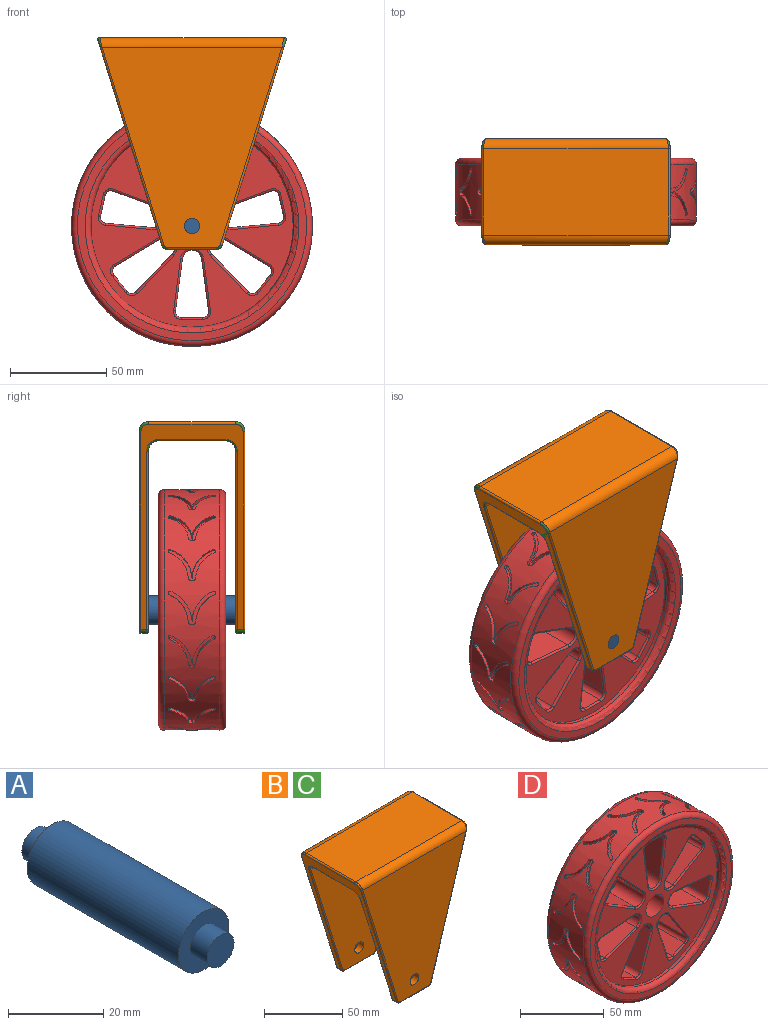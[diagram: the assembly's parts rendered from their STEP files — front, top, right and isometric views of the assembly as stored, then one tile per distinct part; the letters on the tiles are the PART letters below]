
ASSEMBLY  parts=4 mates=2
PART A: 7 faces, bbox 15x55x15 mm
  f0: cylinder r=7.49mm len=45mm, axis (0,1,0), area 2117.7mm2, adj f1,f2
  f1: plane 14.98x14.98mm, normal (0,-1,0), area 126mm2, adj f0,f5
  f2: plane 14.98x14.98mm, normal (0,1,0), area 126mm2, adj f0,f4
  f3: plane 8x8mm, normal (0,1,0), area 50.3mm2, adj f4
  f4: cylinder r=4mm len=8mm, axis (0,1,0), area 125.7mm2, adj f2,f3
  f5: cylinder r=4mm len=8mm, axis (0,1,0), area 125.7mm2, adj f1,f6
  f6: plane 8x8mm, normal (0,-1,0), area 50.3mm2, adj f5
PART B: 52 faces, bbox 98.5x55x110.2 mm
  f0: cylinder r=3mm len=3mm, axis (0,1,0), area 11.4mm2, adj f3,f5,f32,f46
  f1: cylinder r=3mm len=3mm, axis (0,1,0), area 11.4mm2, adj f3,f7,f28,f50
  f2: cylinder r=4.01mm len=8.02mm, axis (0,1,0), area 126mm2, adj f12,f15
  f3: plane 25.52x3mm, normal (0,0,-1), area 76.6mm2, adj f0,f1,f30,f48
  f4: cylinder r=3mm len=3mm, axis (0,1,0), area 11.4mm2, adj f5,f10,f27,f37
  f5: plane 106.6x53mm, normal (0.95,0,-0.3), area 1072.7mm2, adj f0,f4,f29,f31,f33,f34,f35,f36
  f6: plane 95.78x45mm, normal (0,0,1), area 4310mm2, adj f18,f19,f40,f47
  f7: plane 106.6x53mm, normal (-0.95,0,-0.3), area 1072.7mm2, adj f1,f8,f20,f21,f22,f24,f26,f43
  f8: cylinder r=3mm len=3mm, axis (0,1,0), area 11.4mm2, adj f7,f10,f23,f41
  f9: cylinder r=4.01mm len=8.02mm, axis (0,1,0), area 126mm2, adj f11,f14
  f10: plane 25.52x3mm, normal (0,0,-1), area 76.6mm2, adj f4,f8,f25,f39
  f11: plane 104x93.29mm, normal (0,-1,0), area 6279.7mm2, adj f9,f19,f36,f37,f39,f41,f43
  f12: plane 104x93.29mm, normal (0,1,0), area 6279.7mm2, adj f2,f18,f44,f46,f48,f50,f51
  f13: plane 90.79x35mm, normal (0,0,-1), area 3177.7mm2, adj f16,f17,f22,f33
  f14: plane 94x87.05mm, normal (0,1,0), area 5378mm2, adj f9,f17,f21,f23,f25,f27,f29
  f15: plane 94x87.05mm, normal (0,-1,0), area 5378mm2, adj f2,f16,f26,f28,f30,f32,f34
  f16: cylinder r=5mm len=90.79mm, axis (-1,0,0), area 702.4mm2, adj f13,f15,f24,f35
  f17: cylinder r=5mm len=90.79mm, axis (1,0,0), area 702.4mm2, adj f13,f14,f20,f31
  f18: cylinder r=5mm len=95.78mm, axis (-1,0,0), area 745.1mm2, adj f6,f12,f42,f49
  f19: cylinder r=5mm len=95.78mm, axis (1,0,0), area 745.1mm2, adj f6,f11,f38,f45
  f20: bspline ~6x6mm, area 12.1mm2, adj f7,f17,f21,f22
  f21: cylinder r=1mm len=92.89mm, axis (0.3,0,-0.95), area 152.3mm2, adj f7,f14,f20,f23
  f22: cylinder r=1mm len=35mm, axis (0,-1,0), area 44.4mm2, adj f7,f13,f20,f24
  f23: torus R=2mm, axis (0,-1,0), area 5.3mm2, adj f8,f14,f21,f25
  f24: bspline ~6x6mm, area 12.1mm2, adj f7,f16,f22,f26
  f25: cylinder r=1mm len=25.52mm, axis (1,0,0), area 40.1mm2, adj f10,f14,f23,f27
  f26: cylinder r=1mm len=92.89mm, axis (-0.3,0,0.95), area 152.3mm2, adj f7,f15,f24,f28
  f27: torus R=2mm, axis (0,-1,0), area 5.3mm2, adj f4,f14,f25,f29
  f28: torus R=2mm, axis (0,-1,0), area 5.3mm2, adj f1,f15,f26,f30
  f29: cylinder r=1mm len=92.89mm, axis (0.3,0,0.95), area 152.3mm2, adj f5,f14,f27,f31
  f30: cylinder r=1mm len=25.52mm, axis (-1,0,0), area 40.1mm2, adj f3,f15,f28,f32
  f31: bspline ~6x6mm, area 12.1mm2, adj f5,f17,f29,f33
  f32: torus R=2mm, axis (0,-1,0), area 5.3mm2, adj f0,f15,f30,f34
  f33: cylinder r=1mm len=35mm, axis (0,1,0), area 44.4mm2, adj f5,f13,f31,f35
  f34: cylinder r=1mm len=92.89mm, axis (-0.3,0,-0.95), area 152.3mm2, adj f5,f15,f32,f35
  f35: bspline ~6x6mm, area 12.1mm2, adj f5,f16,f33,f34
  f36: cylinder r=1mm len=102.89mm, axis (-0.3,0,-0.95), area 168.8mm2, adj f5,f11,f37,f38
  f37: torus R=2mm, axis (0,-1,0), area 5.3mm2, adj f4,f11,f36,f39
  f38: bspline ~6.14x5.01mm, area 13.2mm2, adj f5,f19,f36,f40
  f39: cylinder r=1mm len=25.52mm, axis (-1,0,0), area 40.1mm2, adj f10,f11,f37,f41
  f40: cylinder r=1mm len=45mm, axis (0,-1,0), area 84.3mm2, adj f5,f6,f38,f42
  f41: torus R=2mm, axis (0,-1,0), area 5.3mm2, adj f8,f11,f39,f43
  f42: bspline ~5.3x5mm, area 13.2mm2, adj f5,f18,f40,f44
  f43: cylinder r=1mm len=102.89mm, axis (-0.3,0,0.95), area 168.8mm2, adj f7,f11,f41,f45
  f44: cylinder r=1mm len=102.89mm, axis (0.3,0,0.95), area 168.8mm2, adj f5,f12,f42,f46
  f45: bspline ~6.14x5.96mm, area 13.2mm2, adj f7,f19,f43,f47
  f46: torus R=2mm, axis (0,-1,0), area 5.3mm2, adj f0,f12,f44,f48
  f47: cylinder r=1mm len=45mm, axis (0,1,0), area 84.3mm2, adj f6,f7,f45,f49
  f48: cylinder r=1mm len=25.52mm, axis (1,0,0), area 40.1mm2, adj f3,f12,f46,f50
  f49: bspline ~6.14x5.01mm, area 13.2mm2, adj f7,f18,f47,f51
  f50: torus R=2mm, axis (0,-1,0), area 5.3mm2, adj f1,f12,f48,f51
  f51: cylinder r=1mm len=102.89mm, axis (0.3,0,-0.95), area 168.8mm2, adj f7,f12,f49,f50
PART C: same geometry as B
PART D: 275 faces, bbox 135.3x35x135.3 mm
  f0: plane 27.26x23mm, normal (0.99,0,0.13), area 632.5mm2, adj f1,f35,f48,f90
  f1: cylinder r=3mm len=23mm, axis (0,1,0), area 117.5mm2, adj f0,f2,f46,f88
  f2: plane 23x11.19mm, normal (0,0,-1), area 257.4mm2, adj f1,f3,f45,f87
  f3: cylinder r=3mm len=23mm, axis (0,1,0), area 117.5mm2, adj f2,f4,f47,f89
  f4: plane 27.26x23mm, normal (-0.99,0,0.13), area 632.5mm2, adj f3,f35,f49,f91
  f5: cylinder r=5mm len=23mm, axis (0,1,0), area 331mm2, adj f6,f36,f55,f97
  f6: plane 23.57x23mm, normal (0.52,0,0.86), area 632.5mm2, adj f5,f7,f53,f95
  f7: cylinder r=3mm len=23mm, axis (0,1,0), area 117.5mm2, adj f6,f8,f51,f93
  f8: plane 23x8.75mm, normal (0.78,0,-0.62), area 257.4mm2, adj f7,f9,f52,f94
  f9: cylinder r=3mm len=23mm, axis (0,1,0), area 117.5mm2, adj f8,f36,f54,f96
  f10: cylinder r=5mm len=23mm, axis (0,1,0), area 331mm2, adj f11,f37,f61,f103
  f11: plane 25.78x23mm, normal (-0.35,0,0.94), area 632.5mm2, adj f10,f12,f59,f101
  f12: cylinder r=3mm len=23mm, axis (0,1,0), area 117.5mm2, adj f11,f13,f57,f99
  f13: plane 23x10.91mm, normal (0.97,0,0.22), area 257.4mm2, adj f12,f14,f58,f100
  f14: cylinder r=3mm len=23mm, axis (0,1,0), area 117.5mm2, adj f13,f37,f60,f102
  f15: cylinder r=5mm len=23mm, axis (0,1,0), area 331mm2, adj f16,f38,f67,f109
  f16: plane 26.13x23mm, normal (-0.95,0,0.31), area 632.5mm2, adj f15,f17,f65,f107
  f17: cylinder r=3mm len=23mm, axis (0,1,0), area 117.5mm2, adj f16,f18,f63,f105
  f18: plane 23x10.08mm, normal (0.43,0,0.9), area 257.4mm2, adj f17,f19,f64,f106
  f19: cylinder r=3mm len=23mm, axis (0,1,0), area 117.5mm2, adj f18,f38,f66,f108
  f20: cylinder r=5mm len=23mm, axis (0,1,0), area 331mm2, adj f21,f39,f73,f115
  f21: plane 23x23mm, normal (-0.84,0,-0.55), area 632.5mm2, adj f20,f22,f71,f113
  f22: cylinder r=3mm len=23mm, axis (0,1,0), area 117.5mm2, adj f21,f23,f69,f111
  f23: plane 23x10.08mm, normal (-0.43,0,0.9), area 257.4mm2, adj f22,f24,f70,f112
  f24: cylinder r=3mm len=23mm, axis (0,1,0), area 117.5mm2, adj f23,f39,f72,f114
  f25: cylinder r=5mm len=23mm, axis (0,1,0), area 331mm2, adj f26,f40,f79,f121
  f26: plane 27.38x23mm, normal (-0.09,0,-1), area 632.5mm2, adj f25,f27,f77,f119
  f27: cylinder r=3mm len=23mm, axis (0,1,0), area 117.5mm2, adj f26,f28,f75,f117
  f28: plane 23x10.91mm, normal (-0.97,0,0.22), area 257.4mm2, adj f27,f29,f76,f118
  f29: cylinder r=3mm len=23mm, axis (0,1,0), area 117.5mm2, adj f28,f40,f78,f120
  f30: cylinder r=5mm len=23mm, axis (0,1,0), area 331mm2, adj f31,f41,f85,f127
  f31: plane 23x19.82mm, normal (0.72,0,-0.69), area 632.5mm2, adj f30,f32,f83,f125
  f32: cylinder r=3mm len=23mm, axis (0,1,0), area 117.5mm2, adj f31,f33,f81,f123
  f33: plane 23x8.75mm, normal (-0.78,0,-0.62), area 257.4mm2, adj f32,f34,f82,f124
  f34: cylinder r=3mm len=23mm, axis (0,1,0), area 117.5mm2, adj f33,f41,f84,f126
  f35: cylinder r=5mm len=23mm, axis (0,1,0), area 331mm2, adj f0,f4,f50,f92
  f36: plane 23x19.82mm, normal (-0.72,0,-0.69), area 632.5mm2, adj f5,f9,f56,f98
  f37: plane 27.38x23mm, normal (0.09,0,-1), area 632.5mm2, adj f10,f14,f62,f104
  f38: plane 23x23mm, normal (0.84,0,-0.55), area 632.5mm2, adj f15,f19,f68,f110
  f39: plane 26.13x23mm, normal (0.95,0,0.31), area 632.5mm2, adj f20,f24,f74,f116
  f40: plane 25.78x23mm, normal (0.35,0,0.94), area 632.5mm2, adj f25,f29,f80,f122
  f41: plane 23.57x23mm, normal (-0.52,0,0.86), area 632.5mm2, adj f30,f34,f86,f128
  f42: cylinder r=7.5mm len=25mm, axis (0,1,0), area 1178.1mm2, adj f43,f44
  f43: plane 105x105mm, normal (0,-1,0), area 4633.1mm2, adj f42,f87,f88,f89,f90,f91,f92,f93
  f44: plane 105x105mm, normal (0,1,0), area 4633.1mm2, adj f42,f45,f46,f47,f48,f49,f50,f51
  f45: cylinder r=1mm len=11.19mm, axis (1,0,0), area 17.6mm2, adj f2,f44,f46,f47
  f46: torus R=4mm, axis (0,-1,0), area 9mm2, adj f1,f44,f45,f48
  f47: torus R=4mm, axis (0,-1,0), area 9mm2, adj f3,f44,f45,f49
  f48: cylinder r=1mm len=27.39mm, axis (-0.13,0,0.99), area 43.2mm2, adj f0,f44,f46,f50
  f49: cylinder r=1mm len=27.39mm, axis (-0.13,0,-0.99), area 43.2mm2, adj f4,f44,f47,f50
  f50: torus R=6mm, axis (0,-1,0), area 24.2mm2, adj f35,f44,f48,f49
  f51: torus R=4mm, axis (0,-1,0), area 9mm2, adj f7,f44,f52,f53
  f52: cylinder r=1mm len=9.37mm, axis (0.62,0,0.78), area 17.6mm2, adj f8,f44,f51,f54
  f53: cylinder r=1mm len=24.08mm, axis (-0.86,0,0.52), area 43.2mm2, adj f6,f44,f51,f55
  f54: torus R=4mm, axis (0,-1,0), area 9mm2, adj f9,f44,f52,f56
  f55: torus R=6mm, axis (0,-1,0), area 24.2mm2, adj f5,f44,f53,f56
  f56: cylinder r=1mm len=20.52mm, axis (0.69,0,-0.72), area 43.2mm2, adj f36,f44,f54,f55
  f57: torus R=4mm, axis (0,-1,0), area 9mm2, adj f12,f44,f58,f59
  f58: cylinder r=1mm len=11.13mm, axis (-0.22,0,0.97), area 17.6mm2, adj f13,f44,f57,f60
  f59: cylinder r=1mm len=26.12mm, axis (-0.94,0,-0.35), area 43.2mm2, adj f11,f44,f57,f61
  f60: torus R=4mm, axis (0,-1,0), area 9mm2, adj f14,f44,f58,f62
  f61: torus R=6mm, axis (0,-1,0), area 24.2mm2, adj f10,f44,f59,f62
  f62: cylinder r=1mm len=27.48mm, axis (1,0,0.09), area 43.2mm2, adj f37,f44,f60,f61
  f63: torus R=4mm, axis (0,-1,0), area 9mm2, adj f17,f44,f64,f65
  f64: cylinder r=1mm len=10.52mm, axis (-0.9,0,0.43), area 17.6mm2, adj f18,f44,f63,f66
  f65: cylinder r=1mm len=26.44mm, axis (-0.31,0,-0.95), area 43.2mm2, adj f16,f44,f63,f67
  f66: torus R=4mm, axis (0,-1,0), area 9mm2, adj f19,f44,f64,f68
  f67: torus R=6mm, axis (0,-1,0), area 24.2mm2, adj f15,f44,f65,f68
  f68: cylinder r=1mm len=23.54mm, axis (0.55,0,0.84), area 43.2mm2, adj f38,f44,f66,f67
  f69: torus R=4mm, axis (0,-1,0), area 9mm2, adj f22,f44,f70,f71
  f70: cylinder r=1mm len=10.52mm, axis (-0.9,0,-0.43), area 17.6mm2, adj f23,f44,f69,f72
  f71: cylinder r=1mm len=23.54mm, axis (0.55,0,-0.84), area 43.2mm2, adj f21,f44,f69,f73
  f72: torus R=4mm, axis (0,-1,0), area 9mm2, adj f24,f44,f70,f74
  f73: torus R=6mm, axis (0,-1,0), area 24.2mm2, adj f20,f44,f71,f74
  f74: cylinder r=1mm len=26.44mm, axis (-0.31,0,0.95), area 43.2mm2, adj f39,f44,f72,f73
  f75: torus R=4mm, axis (0,-1,0), area 9mm2, adj f27,f44,f76,f77
  f76: cylinder r=1mm len=11.13mm, axis (-0.22,0,-0.97), area 17.6mm2, adj f28,f44,f75,f78
  f77: cylinder r=1mm len=27.48mm, axis (1,0,-0.09), area 43.2mm2, adj f26,f44,f75,f79
  f78: torus R=4mm, axis (0,-1,0), area 9mm2, adj f29,f44,f76,f80
  f79: torus R=6mm, axis (0,-1,0), area 24.2mm2, adj f25,f44,f77,f80
  f80: cylinder r=1mm len=26.12mm, axis (-0.94,0,0.35), area 43.2mm2, adj f40,f44,f78,f79
  f81: torus R=4mm, axis (0,-1,0), area 9mm2, adj f32,f44,f82,f83
  f82: cylinder r=1mm len=9.37mm, axis (0.62,0,-0.78), area 17.6mm2, adj f33,f44,f81,f84
  f83: cylinder r=1mm len=20.52mm, axis (0.69,0,0.72), area 43.2mm2, adj f31,f44,f81,f85
  f84: torus R=4mm, axis (0,-1,0), area 9mm2, adj f34,f44,f82,f86
  f85: torus R=6mm, axis (0,-1,0), area 24.2mm2, adj f30,f44,f83,f86
  f86: cylinder r=1mm len=24.08mm, axis (-0.86,0,-0.52), area 43.2mm2, adj f41,f44,f84,f85
  f87: cylinder r=1mm len=11.19mm, axis (-1,0,0), area 17.6mm2, adj f2,f43,f88,f89
  f88: torus R=4mm, axis (0,-1,0), area 9mm2, adj f1,f43,f87,f90
  f89: torus R=4mm, axis (0,-1,0), area 9mm2, adj f3,f43,f87,f91
  f90: cylinder r=1mm len=27.39mm, axis (0.13,0,-0.99), area 43.2mm2, adj f0,f43,f88,f92
  f91: cylinder r=1mm len=27.39mm, axis (0.13,0,0.99), area 43.2mm2, adj f4,f43,f89,f92
  f92: torus R=6mm, axis (0,-1,0), area 24.2mm2, adj f35,f43,f90,f91
  f93: torus R=4mm, axis (0,-1,0), area 9mm2, adj f7,f43,f94,f95
  f94: cylinder r=1mm len=9.37mm, axis (-0.62,0,-0.78), area 17.6mm2, adj f8,f43,f93,f96
  f95: cylinder r=1mm len=24.08mm, axis (0.86,0,-0.52), area 43.2mm2, adj f6,f43,f93,f97
  f96: torus R=4mm, axis (0,-1,0), area 9mm2, adj f9,f43,f94,f98
  f97: torus R=6mm, axis (0,-1,0), area 24.2mm2, adj f5,f43,f95,f98
  f98: cylinder r=1mm len=20.52mm, axis (-0.69,0,0.72), area 43.2mm2, adj f36,f43,f96,f97
  f99: torus R=4mm, axis (0,-1,0), area 9mm2, adj f12,f43,f100,f101
  f100: cylinder r=1mm len=11.13mm, axis (0.22,0,-0.97), area 17.6mm2, adj f13,f43,f99,f102
  f101: cylinder r=1mm len=26.12mm, axis (0.94,0,0.35), area 43.2mm2, adj f11,f43,f99,f103
  f102: torus R=4mm, axis (0,-1,0), area 9mm2, adj f14,f43,f100,f104
  f103: torus R=6mm, axis (0,-1,0), area 24.2mm2, adj f10,f43,f101,f104
  f104: cylinder r=1mm len=27.48mm, axis (-1,0,-0.09), area 43.2mm2, adj f37,f43,f102,f103
  f105: torus R=4mm, axis (0,-1,0), area 9mm2, adj f17,f43,f106,f107
  f106: cylinder r=1mm len=10.52mm, axis (0.9,0,-0.43), area 17.6mm2, adj f18,f43,f105,f108
  f107: cylinder r=1mm len=26.44mm, axis (0.31,0,0.95), area 43.2mm2, adj f16,f43,f105,f109
  f108: torus R=4mm, axis (0,-1,0), area 9mm2, adj f19,f43,f106,f110
  f109: torus R=6mm, axis (0,-1,0), area 24.2mm2, adj f15,f43,f107,f110
  f110: cylinder r=1mm len=23.54mm, axis (-0.55,0,-0.84), area 43.2mm2, adj f38,f43,f108,f109
  f111: torus R=4mm, axis (0,-1,0), area 9mm2, adj f22,f43,f112,f113
  f112: cylinder r=1mm len=10.52mm, axis (0.9,0,0.43), area 17.6mm2, adj f23,f43,f111,f114
  f113: cylinder r=1mm len=23.54mm, axis (-0.55,0,0.84), area 43.2mm2, adj f21,f43,f111,f115
  f114: torus R=4mm, axis (0,-1,0), area 9mm2, adj f24,f43,f112,f116
  f115: torus R=6mm, axis (0,-1,0), area 24.2mm2, adj f20,f43,f113,f116
  f116: cylinder r=1mm len=26.44mm, axis (0.31,0,-0.95), area 43.2mm2, adj f39,f43,f114,f115
  f117: torus R=4mm, axis (0,-1,0), area 9mm2, adj f27,f43,f118,f119
  f118: cylinder r=1mm len=11.13mm, axis (0.22,0,0.97), area 17.6mm2, adj f28,f43,f117,f120
  f119: cylinder r=1mm len=27.48mm, axis (-1,0,0.09), area 43.2mm2, adj f26,f43,f117,f121
  f120: torus R=4mm, axis (0,-1,0), area 9mm2, adj f29,f43,f118,f122
  f121: torus R=6mm, axis (0,-1,0), area 24.2mm2, adj f25,f43,f119,f122
  f122: cylinder r=1mm len=26.12mm, axis (0.94,0,-0.35), area 43.2mm2, adj f40,f43,f120,f121
  f123: torus R=4mm, axis (0,-1,0), area 9mm2, adj f32,f43,f124,f125
  f124: cylinder r=1mm len=9.37mm, axis (-0.62,0,0.78), area 17.6mm2, adj f33,f43,f123,f126
  f125: cylinder r=1mm len=20.52mm, axis (-0.69,0,-0.72), area 43.2mm2, adj f31,f43,f123,f127
  f126: torus R=4mm, axis (0,-1,0), area 9mm2, adj f34,f43,f124,f128
  f127: torus R=6mm, axis (0,-1,0), area 24.2mm2, adj f30,f43,f125,f128
  f128: cylinder r=1mm len=24.08mm, axis (0.86,0,0.52), area 43.2mm2, adj f41,f43,f126,f127
  f129: cylinder r=52.5mm len=105mm, axis (0,1,0), area 659.7mm2, adj f43,f137
  f130: cylinder r=52.5mm len=105mm, axis (0,1,0), area 659.7mm2, adj f44,f135
  f131: cylinder r=62.5mm len=125mm, axis (0,1,0), area 9902.6mm2, adj f132,f136,f138,f139,f140,f141,f142,f143
  f132: cylinder r=62.5mm len=11.48mm, axis (0,1,0), area 40.4mm2, adj f131,f182,f184
  f133: plane 119x119mm, normal (0,-1,0), area 1445.1mm2, adj f137,f138
  f134: plane 119x119mm, normal (0,1,0), area 1445.1mm2, adj f135,f136
  f135: torus R=55.5mm, axis (0,-1,0), area 1586.7mm2, adj f130,f134
  f136: torus R=59.5mm, axis (0,-1,0), area 1818.3mm2, adj f131,f134
  f137: torus R=55.5mm, axis (0,-1,0), area 1586.7mm2, adj f129,f133
  f138: torus R=59.5mm, axis (0,-1,0), area 1818.3mm2, adj f131,f133
  f139: cylinder r=2mm len=3.99mm, axis (0,0,1), area 12mm2, adj f131,f140,f143,f146
  f140: cylinder r=16mm len=13.68mm, axis (0,0,1), area 35.2mm2, adj f131,f139,f141,f146
  f141: cylinder r=1mm len=2.46mm, axis (0,0,1), area 6.3mm2, adj f131,f140,f142,f146
  f142: cylinder r=18mm len=15.39mm, axis (0,0,1), area 39.6mm2, adj f131,f141,f144,f146
  f143: cylinder r=16mm len=13.68mm, axis (0,0,1), area 35.4mm2, adj f131,f139,f145,f146
  f144: cylinder r=18mm len=15.39mm, axis (0,0,1), area 39.8mm2, adj f131,f142,f145,f146
  f145: cylinder r=1mm len=2.46mm, axis (0,0,1), area 6.2mm2, adj f131,f143,f144,f146
  f146: cylinder r=62.5mm len=24.56mm, axis (0,1,0), area 85mm2, adj f139,f140,f141,f142,f143,f144,f145
  f147: cylinder r=2mm len=3.99mm, axis (-1,0,0.09), area 12mm2, adj f131,f148,f151,f154
  f148: cylinder r=16mm len=13.94mm, axis (-1,0,0.09), area 35.2mm2, adj f131,f147,f149,f154
  f149: cylinder r=1mm len=2.62mm, axis (-1,0,0.09), area 6.3mm2, adj f131,f148,f150,f154
  f150: cylinder r=18mm len=15.68mm, axis (-1,0,0.09), area 39.6mm2, adj f131,f149,f152,f154
  f151: cylinder r=16mm len=13.94mm, axis (-1,0,0.09), area 35.4mm2, adj f131,f147,f153,f154
  f152: cylinder r=18mm len=15.68mm, axis (-1,0,0.09), area 39.8mm2, adj f131,f150,f153,f154
  f153: cylinder r=1mm len=2.62mm, axis (-1,0,0.09), area 6.2mm2, adj f131,f151,f152,f154
  f154: cylinder r=62.5mm len=24.56mm, axis (0,1,0), area 85mm2, adj f147,f148,f149,f150,f151,f152,f153
  f155: cylinder r=2mm len=3.99mm, axis (-0.9,0,0.45), area 12mm2, adj f131,f156,f159,f162
  f156: cylinder r=16mm len=13.8mm, axis (-0.9,0,0.45), area 35.2mm2, adj f131,f155,f157,f162
  f157: cylinder r=1mm len=3.05mm, axis (-0.9,0,0.45), area 6.3mm2, adj f131,f156,f158,f162
  f158: cylinder r=18mm len=15.52mm, axis (-0.9,0,0.45), area 39.6mm2, adj f131,f157,f160,f162
  f159: cylinder r=16mm len=13.8mm, axis (-0.9,0,0.45), area 35.4mm2, adj f131,f155,f161,f162
  f160: cylinder r=18mm len=15.52mm, axis (-0.9,0,0.45), area 39.8mm2, adj f131,f158,f161,f162
  f161: cylinder r=1mm len=3.05mm, axis (-0.9,0,0.45), area 6.2mm2, adj f131,f159,f160,f162
  f162: cylinder r=62.5mm len=24.56mm, axis (0,1,0), area 85mm2, adj f155,f156,f157,f158,f159,f160,f161
  f163: cylinder r=2mm len=3.99mm, axis (-0.36,0,0.93), area 12mm2, adj f131,f164,f167,f170
  f164: cylinder r=16mm len=14.01mm, axis (-0.36,0,0.93), area 35.2mm2, adj f131,f163,f165,f170
  f165: cylinder r=1mm len=2.98mm, axis (-0.36,0,0.93), area 6.3mm2, adj f131,f164,f166,f170
  f166: cylinder r=18mm len=15.77mm, axis (-0.36,0,0.93), area 39.6mm2, adj f131,f165,f168,f170
  f167: cylinder r=16mm len=14.01mm, axis (-0.36,0,0.93), area 35.4mm2, adj f131,f163,f169,f170
  f168: cylinder r=18mm len=15.77mm, axis (-0.36,0,0.93), area 39.8mm2, adj f131,f166,f169,f170
  f169: cylinder r=1mm len=2.98mm, axis (-0.36,0,0.93), area 6.2mm2, adj f131,f167,f168,f170
  f170: cylinder r=62.5mm len=24.56mm, axis (0,1,0), area 85mm2, adj f163,f164,f165,f166,f167,f168,f169
  f171: cylinder r=2mm len=3.99mm, axis (-0.67,0,0.74), area 12mm2, adj f131,f172,f175,f178
  f172: cylinder r=16mm len=12.46mm, axis (-0.67,0,0.74), area 35.2mm2, adj f131,f171,f173,f178
  f173: cylinder r=1mm len=3.11mm, axis (-0.67,0,0.74), area 6.3mm2, adj f131,f172,f174,f178
  f174: cylinder r=18mm len=14.02mm, axis (-0.67,0,0.74), area 39.6mm2, adj f131,f173,f176,f178
  f175: cylinder r=16mm len=12.46mm, axis (-0.67,0,0.74), area 35.4mm2, adj f131,f171,f177,f178
  f176: cylinder r=18mm len=14.02mm, axis (-0.67,0,0.74), area 39.8mm2, adj f131,f174,f177,f178
  f177: cylinder r=1mm len=3.11mm, axis (-0.67,0,0.74), area 6.2mm2, adj f131,f175,f176,f178
  f178: cylinder r=62.5mm len=24.56mm, axis (0,1,0), area 85mm2, adj f171,f172,f173,f174,f175,f176,f177
  f179: cylinder r=2mm len=3.99mm, axis (-0.18,0,-0.98), area 12mm2, adj f131,f180,f183,f186
  f180: cylinder r=16mm len=14.09mm, axis (-0.18,0,-0.98), area 35.2mm2, adj f131,f179,f181,f186
  f181: cylinder r=1mm len=2.77mm, axis (-0.18,0,-0.98), area 6.3mm2, adj f131,f180,f182,f186
  f182: cylinder r=18mm len=15.85mm, axis (-0.18,0,-0.98), area 39.6mm2, adj f131,f132,f181,f184,f186
  f183: cylinder r=16mm len=14.09mm, axis (-0.18,0,-0.98), area 35.4mm2, adj f131,f179,f185,f186
  f184: cylinder r=18mm len=15.85mm, axis (-0.18,0,-0.98), area 39.8mm2, adj f131,f132,f182,f185,f186
  f185: cylinder r=1mm len=2.77mm, axis (-0.18,0,-0.98), area 6.2mm2, adj f131,f183,f184,f186
  f186: cylinder r=62.5mm len=24.56mm, axis (0,1,0), area 85mm2, adj f179,f180,f181,f182,f183,f184,f185
  f187: cylinder r=2mm len=3.99mm, axis (-0.53,0,-0.85), area 12mm2, adj f131,f188,f191,f194
  f188: cylinder r=16mm len=13.47mm, axis (-0.53,0,-0.85), area 35.2mm2, adj f131,f187,f189,f194
  f189: cylinder r=1mm len=3.1mm, axis (-0.53,0,-0.85), area 6.3mm2, adj f131,f188,f190,f194
  f190: cylinder r=18mm len=15.15mm, axis (-0.53,0,-0.85), area 39.6mm2, adj f131,f189,f192,f194
  f191: cylinder r=16mm len=13.46mm, axis (-0.53,0,-0.85), area 35.4mm2, adj f131,f187,f193,f194
  f192: cylinder r=18mm len=15.15mm, axis (-0.53,0,-0.85), area 39.8mm2, adj f131,f190,f193,f194
  f193: cylinder r=1mm len=3.1mm, axis (-0.53,0,-0.85), area 6.2mm2, adj f131,f191,f192,f194
  f194: cylinder r=62.5mm len=24.56mm, axis (0,1,0), area 85mm2, adj f187,f188,f189,f190,f191,f192,f193
  f195: cylinder r=2mm len=3.99mm, axis (-0.96,0,-0.27), area 12mm2, adj f131,f196,f199,f202
  f196: cylinder r=16mm len=14.11mm, axis (-0.96,0,-0.27), area 35.2mm2, adj f131,f195,f197,f202
  f197: cylinder r=1mm len=2.89mm, axis (-0.96,0,-0.27), area 6.3mm2, adj f131,f196,f198,f202
  f198: cylinder r=18mm len=15.87mm, axis (-0.96,0,-0.27), area 39.6mm2, adj f131,f197,f200,f202
  f199: cylinder r=16mm len=14.11mm, axis (-0.96,0,-0.27), area 35.4mm2, adj f131,f195,f201,f202
  f200: cylinder r=18mm len=15.87mm, axis (-0.96,0,-0.27), area 39.8mm2, adj f131,f198,f201,f202
  f201: cylinder r=1mm len=2.89mm, axis (-0.96,0,-0.27), area 6.2mm2, adj f131,f199,f200,f202
  f202: cylinder r=62.5mm len=24.56mm, axis (0,1,0), area 85mm2, adj f195,f196,f197,f198,f199,f200,f201
  f203: cylinder r=2mm len=3.99mm, axis (-0.8,0,-0.6), area 12mm2, adj f131,f204,f207,f210
  f204: cylinder r=16mm len=13.02mm, axis (-0.8,0,-0.6), area 35.2mm2, adj f131,f203,f205,f210
  f205: cylinder r=1mm len=3.12mm, axis (-0.8,0,-0.6), area 6.3mm2, adj f131,f204,f206,f210
  f206: cylinder r=18mm len=14.64mm, axis (-0.8,0,-0.6), area 39.6mm2, adj f131,f205,f208,f210
  f207: cylinder r=16mm len=13.02mm, axis (-0.8,0,-0.6), area 35.4mm2, adj f131,f203,f209,f210
  f208: cylinder r=18mm len=14.64mm, axis (-0.8,0,-0.6), area 39.8mm2, adj f131,f206,f209,f210
  f209: cylinder r=1mm len=3.12mm, axis (-0.8,0,-0.6), area 6.2mm2, adj f131,f207,f208,f210
  f210: cylinder r=62.5mm len=24.56mm, axis (0,1,0), area 85mm2, adj f203,f204,f205,f206,f207,f208,f209
  f211: cylinder r=2mm len=3.99mm, axis (0.8,0,-0.6), area 12mm2, adj f131,f212,f215,f218
  f212: cylinder r=16mm len=13.02mm, axis (0.8,0,-0.6), area 35.2mm2, adj f131,f211,f213,f218
  f213: cylinder r=1mm len=3.12mm, axis (0.8,0,-0.6), area 6.3mm2, adj f131,f212,f214,f218
  f214: cylinder r=18mm len=14.64mm, axis (0.8,0,-0.6), area 39.6mm2, adj f131,f213,f216,f218
  f215: cylinder r=16mm len=13.02mm, axis (0.8,0,-0.6), area 35.4mm2, adj f131,f211,f217,f218
  f216: cylinder r=18mm len=14.64mm, axis (0.8,0,-0.6), area 39.8mm2, adj f131,f214,f217,f218
  f217: cylinder r=1mm len=3.12mm, axis (0.8,0,-0.6), area 6.2mm2, adj f131,f215,f216,f218
  f218: cylinder r=62.5mm len=24.56mm, axis (0,1,0), area 85mm2, adj f211,f212,f213,f214,f215,f216,f217
  f219: cylinder r=2mm len=3.99mm, axis (0.96,0,-0.27), area 12mm2, adj f131,f220,f223,f226
  f220: cylinder r=16mm len=14.11mm, axis (0.96,0,-0.27), area 35.2mm2, adj f131,f219,f221,f226
  f221: cylinder r=1mm len=2.89mm, axis (0.96,0,-0.27), area 6.3mm2, adj f131,f220,f222,f226
  f222: cylinder r=18mm len=15.87mm, axis (0.96,0,-0.27), area 39.6mm2, adj f131,f221,f224,f226
  f223: cylinder r=16mm len=14.11mm, axis (0.96,0,-0.27), area 35.4mm2, adj f131,f219,f225,f226
  f224: cylinder r=18mm len=15.87mm, axis (0.96,0,-0.27), area 39.8mm2, adj f131,f222,f225,f226
  f225: cylinder r=1mm len=2.89mm, axis (0.96,0,-0.27), area 6.2mm2, adj f131,f223,f224,f226
  f226: cylinder r=62.5mm len=24.56mm, axis (0,1,0), area 85mm2, adj f219,f220,f221,f222,f223,f224,f225
  f227: cylinder r=2mm len=3.99mm, axis (0.53,0,-0.85), area 12mm2, adj f131,f228,f231,f234
  f228: cylinder r=16mm len=13.47mm, axis (0.53,0,-0.85), area 35.2mm2, adj f131,f227,f229,f234
  f229: cylinder r=1mm len=3.1mm, axis (0.53,0,-0.85), area 6.3mm2, adj f131,f228,f230,f234
  f230: cylinder r=18mm len=15.15mm, axis (0.53,0,-0.85), area 39.6mm2, adj f131,f229,f232,f234
  f231: cylinder r=16mm len=13.46mm, axis (0.53,0,-0.85), area 35.4mm2, adj f131,f227,f233,f234
  f232: cylinder r=18mm len=15.15mm, axis (0.53,0,-0.85), area 39.8mm2, adj f131,f230,f233,f234
  f233: cylinder r=1mm len=3.1mm, axis (0.53,0,-0.85), area 6.2mm2, adj f131,f231,f232,f234
  f234: cylinder r=62.5mm len=24.56mm, axis (0,1,0), area 85mm2, adj f227,f228,f229,f230,f231,f232,f233
  f235: cylinder r=2mm len=3.99mm, axis (0.18,0,-0.98), area 12mm2, adj f131,f236,f239,f242
  f236: cylinder r=16mm len=14.09mm, axis (0.18,0,-0.98), area 35.2mm2, adj f131,f235,f237,f242
  f237: cylinder r=1mm len=2.77mm, axis (0.18,0,-0.98), area 6.3mm2, adj f131,f236,f238,f242
  f238: cylinder r=18mm len=15.85mm, axis (0.18,0,-0.98), area 39.6mm2, adj f131,f237,f240,f242
  f239: cylinder r=16mm len=14.09mm, axis (0.18,0,-0.98), area 35.4mm2, adj f131,f235,f241,f242
  f240: cylinder r=18mm len=15.85mm, axis (0.18,0,-0.98), area 39.8mm2, adj f131,f238,f241,f242
  f241: cylinder r=1mm len=2.77mm, axis (0.18,0,-0.98), area 6.2mm2, adj f131,f239,f240,f242
  f242: cylinder r=62.5mm len=24.56mm, axis (0,1,0), area 85mm2, adj f235,f236,f237,f238,f239,f240,f241
  f243: cylinder r=2mm len=3.99mm, axis (0.67,0,0.74), area 12mm2, adj f131,f244,f247,f250
  f244: cylinder r=16mm len=12.46mm, axis (0.67,0,0.74), area 35.2mm2, adj f131,f243,f245,f250
  f245: cylinder r=1mm len=3.11mm, axis (0.67,0,0.74), area 6.3mm2, adj f131,f244,f246,f250
  f246: cylinder r=18mm len=14.02mm, axis (0.67,0,0.74), area 39.6mm2, adj f131,f245,f248,f250
  f247: cylinder r=16mm len=12.46mm, axis (0.67,0,0.74), area 35.4mm2, adj f131,f243,f249,f250
  f248: cylinder r=18mm len=14.02mm, axis (0.67,0,0.74), area 39.8mm2, adj f131,f246,f249,f250
  f249: cylinder r=1mm len=3.11mm, axis (0.67,0,0.74), area 6.2mm2, adj f131,f247,f248,f250
  f250: cylinder r=62.5mm len=24.56mm, axis (0,1,0), area 85mm2, adj f243,f244,f245,f246,f247,f248,f249
  f251: cylinder r=2mm len=3.99mm, axis (0.36,0,0.93), area 12mm2, adj f131,f252,f255,f258
  f252: cylinder r=16mm len=14.01mm, axis (0.36,0,0.93), area 35.2mm2, adj f131,f251,f253,f258
  f253: cylinder r=1mm len=2.98mm, axis (0.36,0,0.93), area 6.3mm2, adj f131,f252,f254,f258
  f254: cylinder r=18mm len=15.77mm, axis (0.36,0,0.93), area 39.6mm2, adj f131,f253,f256,f258
  f255: cylinder r=16mm len=14.01mm, axis (0.36,0,0.93), area 35.4mm2, adj f131,f251,f257,f258
  f256: cylinder r=18mm len=15.77mm, axis (0.36,0,0.93), area 39.8mm2, adj f131,f254,f257,f258
  f257: cylinder r=1mm len=2.98mm, axis (0.36,0,0.93), area 6.2mm2, adj f131,f255,f256,f258
  f258: cylinder r=62.5mm len=24.56mm, axis (0,1,0), area 85mm2, adj f251,f252,f253,f254,f255,f256,f257
  f259: cylinder r=2mm len=3.99mm, axis (0.9,0,0.45), area 12mm2, adj f131,f260,f263,f266
  f260: cylinder r=16mm len=13.8mm, axis (0.9,0,0.45), area 35.2mm2, adj f131,f259,f261,f266
  f261: cylinder r=1mm len=3.06mm, axis (0.9,0,0.45), area 6.3mm2, adj f131,f260,f262,f266
  f262: cylinder r=18mm len=15.52mm, axis (0.9,0,0.45), area 39.6mm2, adj f131,f261,f264,f266
  f263: cylinder r=16mm len=13.8mm, axis (0.9,0,0.45), area 35.4mm2, adj f131,f259,f265,f266
  f264: cylinder r=18mm len=15.52mm, axis (0.9,0,0.45), area 39.8mm2, adj f131,f262,f265,f266
  f265: cylinder r=1mm len=3.05mm, axis (0.9,0,0.45), area 6.2mm2, adj f131,f263,f264,f266
  f266: cylinder r=62.5mm len=24.56mm, axis (0,1,0), area 85mm2, adj f259,f260,f261,f262,f263,f264,f265
  f267: cylinder r=2mm len=3.99mm, axis (1,0,0.09), area 12mm2, adj f131,f268,f271,f274
  f268: cylinder r=16mm len=13.94mm, axis (1,0,0.09), area 35.2mm2, adj f131,f267,f269,f274
  f269: cylinder r=1mm len=2.62mm, axis (1,0,0.09), area 6.3mm2, adj f131,f268,f270,f274
  f270: cylinder r=18mm len=15.68mm, axis (1,0,0.09), area 39.6mm2, adj f131,f269,f272,f274
  f271: cylinder r=16mm len=13.94mm, axis (1,0,0.09), area 35.4mm2, adj f131,f267,f273,f274
  f272: cylinder r=18mm len=15.68mm, axis (1,0,0.09), area 39.8mm2, adj f131,f270,f273,f274
  f273: cylinder r=1mm len=2.62mm, axis (1,0,0.09), area 6.2mm2, adj f131,f271,f272,f274
  f274: cylinder r=62.5mm len=24.56mm, axis (0,1,0), area 85mm2, adj f267,f268,f269,f270,f271,f272,f273
PLACE A rot(axis=(1,0,0),180deg) t=(35.25,-124.32,-57.32)mm
PLACE B t=(35.25,-124.32,-57.32)mm
PLACE C t=(35.25,-124.32,-57.32)mm
PLACE D rot(axis=(1,0,0),180deg) t=(35.25,-124.32,-57.32)mm
MATE fastened A.f0 <-> D.f42  axis (0,-1,0) through (35.25,-124.32,-57.32)mm
MATE revolute A.f0 <-> B.f2  axis (0,-1,0) through (35.25,-151.82,-57.32)mm
